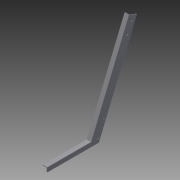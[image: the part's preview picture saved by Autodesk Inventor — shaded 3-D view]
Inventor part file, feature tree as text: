
AUTODESK INVENTOR PART (.ipt)
format: ipt  version: 2013 (Build 170138000, 138)  size: 114,176 bytes
history: native  units: in
note: dims shown in document units (in); Inventor stores cm internally (conversion verified against a paired STEP export)
features: extrude x2, sketch x2
ambient origin geometry x8: Origin, YZ Plane, XZ Plane, XY Plane, X Axis, Y Axis, Z Axis, Center Point
bodies: Solid1 (feature_tree)
feature tree (4):
  extrude  "Extrusion1"  TaperAngle=90.0deg  [1 undecoded]
  extrude  "Extrusion2"  TaperAngle=22.5deg  [1 undecoded]
  sketch  "Sketch1"  dims[d0=10.0in d1=90.0deg]
  sketch  "Sketch2"  dims[d2=22.5in d3=22.5deg d4=1.0in d5=180.0deg d6=2.0in d7=112.5deg d8=22.5in d9=90.0deg d12=90.0deg d17=0.5in d18=0.5in d19=0.5in d20=6.0in d22=0.5in d26=0.25in d27=0.25in d28=0.125in d29=0.0in d30=0.125in d31=22.5deg d33=0.125in d34=90.0deg d35=90.0deg d36=1.0in d37=0.0in]
note: 2 required parameter values undecoded (feature->parameter linkage not recoverable at this tier; creation-order binding heuristic only, values carry confidence <= 0.55)
